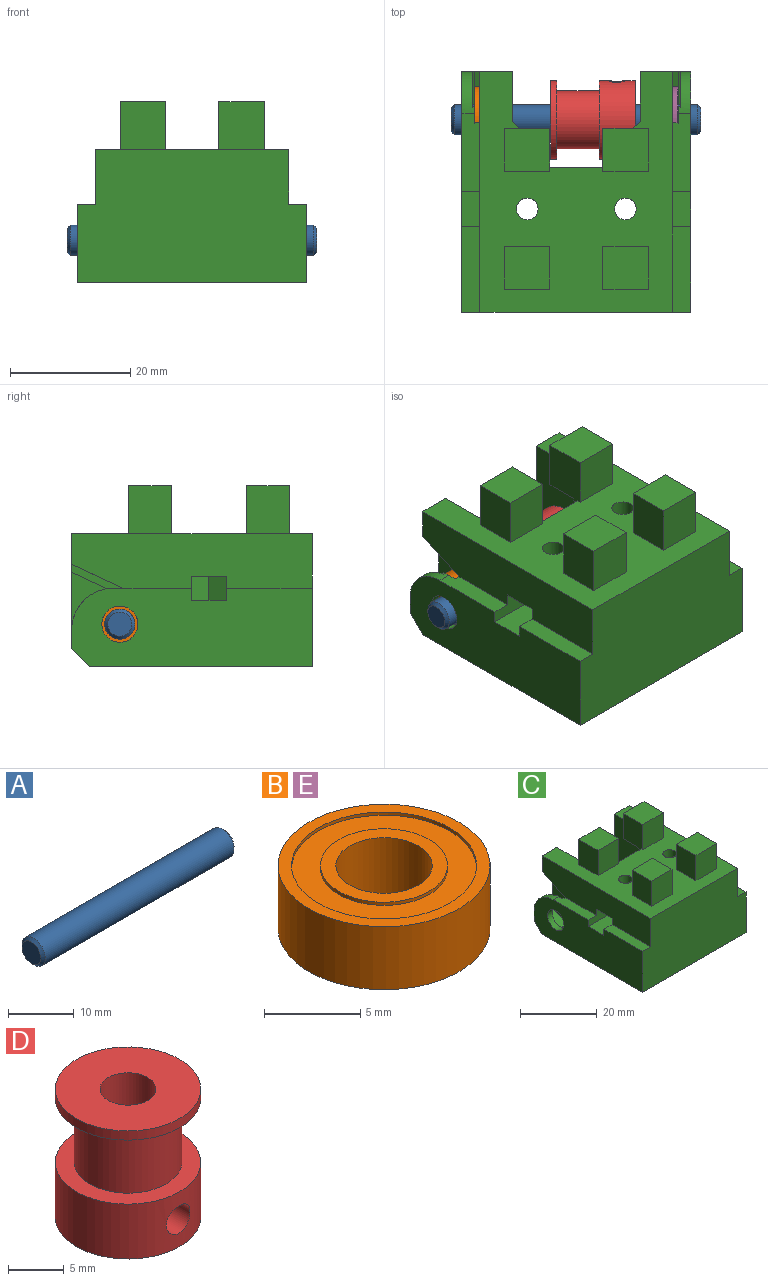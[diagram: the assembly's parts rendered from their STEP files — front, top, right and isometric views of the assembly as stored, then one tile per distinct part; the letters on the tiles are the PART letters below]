
ASSEMBLY  parts=5 mates=5
PART A: 5 faces, bbox 41.5x5x5 mm
  f0: cylinder r=2.5mm len=40.5mm, axis (-1,0,0), area 636.2mm2, adj f3,f4
  f1: plane 4x4mm, normal (1,0,0), area 12.6mm2, adj f3
  f2: plane 4x4mm, normal (-1,0,0), area 12.6mm2, adj f4
  f3: cone r=2mm half-angle=45deg, axis (-1,0,0), area 10mm2, adj f0,f1
  f4: cone r=2.5mm half-angle=45deg, axis (1,0,0), area 10mm2, adj f0,f2
PART B: 12 faces, bbox 11x11x4 mm
  f0: plane 6.6x6.6mm, normal (0,0,1), area 14.6mm2, adj f3,f9
  f1: plane 6.6x6.6mm, normal (0,0,-1), area 14.6mm2, adj f3,f6
  f2: cylinder r=5.5mm len=11mm, axis (0,0,-1), area 138.2mm2, adj f4,f5
  f3: cylinder r=2.5mm len=5mm, axis (0,0,-1), area 62.8mm2, adj f0,f1
  f4: plane 11x11mm, normal (0,0,1), area 22.7mm2, adj f2,f10
  f5: plane 11x11mm, normal (0,0,-1), area 22.7mm2, adj f2,f7
  f6: cylinder r=3.3mm len=6.6mm, axis (0,0,-1), area 4.1mm2, adj f1,f8
  f7: cylinder r=4.8mm len=9.6mm, axis (0,0,-1), area 6mm2, adj f5,f8
  f8: plane 9.6x9.6mm, normal (0,0,-1), area 38.2mm2, adj f6,f7
  f9: cylinder r=3.3mm len=6.6mm, axis (0,0,-1), area 4.1mm2, adj f0,f11
  f10: cylinder r=4.8mm len=9.6mm, axis (0,0,-1), area 6mm2, adj f4,f11
  f11: plane 9.6x9.6mm, normal (0,0,1), area 38.2mm2, adj f9,f10
PART C: 107 faces, bbox 38x40x30 mm
  f0: plane 39.96x13mm, normal (-1,0,0), area 464.6mm2, adj f3,f11,f15,f18,f72,f77,f80,f100
  f1: cylinder r=1.8mm len=7mm, axis (0,0,-1), area 79.2mm2, adj f5,f97
  f2: cylinder r=1.8mm len=7mm, axis (0,0,-1), area 79.2mm2, adj f5,f99
  f3: plane 12.9x3mm, normal (0,0,1), area 37.3mm2, adj f0,f8,f55,f76,f100,f105
  f4: plane 12.9x3mm, normal (0,0,1), area 37.3mm2, adj f6,f50,f53,f78,f94,f106
  f5: plane 39.96x32mm, normal (0,0,1), area 785.9mm2, adj f1,f2,f7,f11,f12,f13,f14,f15
  f6: plane 39.96x13mm, normal (1,0,0), area 464.6mm2, adj f4,f7,f15,f18,f75,f79,f81,f94
  f7: plane 19x8.4mm, normal (0,1,0), area 61.1mm2, adj f5,f6,f12,f49,f50,f52,f53,f58
  f8: plane 13.65x11.65mm, normal (1,0,0), area 30.5mm2, adj f3,f9,f11,f54,f55,f56,f70,f71
  f9: plane 4.02x1.87mm, normal (0,0.42,-0.91), area 1.8mm2, adj f8,f10,f70,f105
  f10: plane 12.45x10.36mm, normal (1,0,0), area 65.5mm2, adj f9,f11,f70,f71,f72,f105
  f11: plane 19x8.4mm, normal (0,1,0), area 61.1mm2, adj f0,f5,f8,f10,f14,f54,f55,f57
  f12: plane 20.8x16mm, normal (-1,0,0), area 289.1mm2, adj f5,f7,f13,f74,f82,f83,f88,f91
  f13: plane 21.2x20.8mm, normal (0,1,0), area 426.1mm2, adj f5,f12,f14,f31,f36,f84,f87,f89
  f14: plane 20.8x16mm, normal (1,0,0), area 289.1mm2, adj f5,f11,f13,f73,f85,f86,f90,f92
  f15: plane 38x22mm, normal (0,-1,0), area 782mm2, adj f0,f5,f6,f18,f76,f77,f78,f79
  f16: cylinder r=1.8mm len=11mm, axis (0,0,-1), area 124.4mm2, adj f18,f98
  f17: cylinder r=1.8mm len=11mm, axis (0,0,-1), area 124.4mm2, adj f18,f104
  f18: plane 38x36.96mm, normal (0,0,-1), area 803.8mm2, adj f0,f6,f15,f16,f17,f41,f42,f43
  f19: plane 8x7.6mm, normal (0,1,0), area 60.8mm2, adj f5,f20,f22,f23
  f20: plane 8x7.1mm, normal (-1,0,0), area 56.8mm2, adj f5,f19,f21,f23
  f21: plane 8x7.6mm, normal (0,-1,0), area 60.8mm2, adj f5,f20,f22,f23
  f22: plane 8x7.1mm, normal (1,0,0), area 56.8mm2, adj f5,f19,f21,f23
  f23: plane 7.6x7.1mm, normal (0,0,1), area 54mm2, adj f19,f20,f21,f22
  f24: plane 8x7.6mm, normal (0,1,0), area 60.8mm2, adj f5,f25,f27,f28
  f25: plane 8x7.1mm, normal (-1,0,0), area 56.8mm2, adj f5,f24,f26,f28
  f26: plane 8x7.6mm, normal (0,-1,0), area 60.8mm2, adj f5,f25,f27,f28
  f27: plane 8x7.1mm, normal (1,0,0), area 56.8mm2, adj f5,f24,f26,f28
  f28: plane 7.6x7.1mm, normal (0,0,1), area 54mm2, adj f24,f25,f26,f27
  f29: plane 5.35x5mm, normal (0,0,-1), area 26.7mm2, adj f30,f31,f87,f88
  f30: plane 8x7.6mm, normal (0,1,0), area 60.8mm2, adj f5,f29,f31,f33,f34
  f31: plane 9.2x7.1mm, normal (-1,0,0), area 57.5mm2, adj f5,f13,f29,f30,f32,f34,f87
  f32: plane 8x7.6mm, normal (0,-1,0), area 60.8mm2, adj f5,f31,f33,f34
  f33: plane 8x7.1mm, normal (1,0,0), area 56.8mm2, adj f5,f30,f32,f34
  f34: plane 7.6x7.1mm, normal (0,0,1), area 54mm2, adj f30,f31,f32,f33
  f35: plane 8x7.6mm, normal (0,-1,0), area 60.8mm2, adj f5,f36,f38,f39
  f36: plane 9.2x7.1mm, normal (1,0,0), area 57.5mm2, adj f5,f13,f35,f37,f39,f40,f89
  f37: plane 8x7.6mm, normal (0,1,0), area 60.8mm2, adj f5,f36,f38,f39,f40
  f38: plane 8x7.1mm, normal (-1,0,0), area 56.8mm2, adj f5,f35,f37,f39
  f39: plane 7.6x7.1mm, normal (0,0,1), area 54mm2, adj f35,f36,f37,f38
  f40: plane 5.35x5mm, normal (0,0,-1), area 26.8mm2, adj f36,f37,f89,f90
  f41: plane 20x15mm, normal (0.47,0.88,0), area 339.8mm2, adj f18,f42,f47,f48
  f42: plane 20x8.39mm, normal (0.38,-0.92,0), area 181.6mm2, adj f18,f41,f43,f48
  f43: cylinder r=4mm len=20mm, axis (0,0,-1), area 46mm2, adj f18,f42,f44,f48
  f44: plane 20x7.07mm, normal (0.82,-0.57,0), area 171.4mm2, adj f18,f43,f45,f48
  f45: plane 20x8.04mm, normal (-0.82,-0.57,0), area 195.1mm2, adj f18,f44,f46,f48
  f46: plane 20x9.48mm, normal (-0.38,-0.92,0), area 205.3mm2, adj f18,f45,f47,f48
  f47: plane 20x15mm, normal (-0.47,0.88,0), area 339.8mm2, adj f18,f41,f46,f48
  f48: plane 30x19.96mm, normal (0,0,-1), area 245mm2, adj f41,f42,f43,f44,f45,f46,f47
  f49: plane 6.07x4.2mm, normal (0,-0.34,0.94), area 27.1mm2, adj f7,f51,f52,f53
  f50: plane 10.39x4.84mm, normal (0,0.42,-0.91), area 39.7mm2, adj f4,f7,f51,f52,f53,f78
  f51: cylinder r=5.65mm len=10.77mm, axis (1,0,0), area 72.5mm2, adj f49,f50,f52,f53
  f52: plane 15.61x13.65mm, normal (1,0,0), area 39.9mm2, adj f7,f49,f50,f51,f62,f63,f64
  f53: plane 13.65x11.65mm, normal (-1,0,0), area 30.5mm2, adj f4,f7,f49,f50,f51,f58,f59,f60
  f54: plane 6.07x4.2mm, normal (0,-0.34,0.94), area 27.1mm2, adj f8,f11,f56,f57
  f55: plane 10.39x4.84mm, normal (0,0.42,-0.91), area 39.7mm2, adj f3,f8,f11,f56,f57,f76
  f56: cylinder r=5.65mm len=10.77mm, axis (1,0,0), area 72.5mm2, adj f8,f54,f55,f57
  f57: plane 15.61x13.65mm, normal (-1,0,0), area 39.9mm2, adj f11,f54,f55,f56,f66,f67,f68
  f58: plane 6.48x2.36mm, normal (0,-0.34,0.94), area 2.8mm2, adj f7,f53,f59,f61
  f59: cylinder r=4.45mm len=8.48mm, axis (1,0,0), area 5.4mm2, adj f53,f58,f60,f61
  f60: plane 4.02x1.87mm, normal (0,0.42,-0.91), area 1.8mm2, adj f53,f59,f61,f106
  f61: plane 12.45x10.36mm, normal (-1,0,0), area 65.5mm2, adj f7,f58,f59,f60,f75,f106
  f62: plane 9.88x4.61mm, normal (0,0.42,-0.91), area 4.4mm2, adj f7,f52,f63,f65
  f63: cylinder r=4.45mm len=8.48mm, axis (1,0,0), area 5.4mm2, adj f52,f62,f64,f65
  f64: plane 6.48x2.36mm, normal (0,-0.34,0.94), area 2.8mm2, adj f7,f52,f63,f65
  f65: plane 13.09x12.45mm, normal (1,0,0), area 83.4mm2, adj f7,f62,f63,f64,f74
  f66: plane 6.48x2.36mm, normal (0,-0.34,0.94), area 2.8mm2, adj f11,f57,f67,f69
  f67: cylinder r=4.45mm len=8.48mm, axis (1,0,0), area 5.4mm2, adj f57,f66,f68,f69
  f68: plane 9.88x4.61mm, normal (0,0.42,-0.91), area 4.4mm2, adj f11,f57,f67,f69
  f69: plane 13.09x12.45mm, normal (-1,0,0), area 83.4mm2, adj f11,f66,f67,f68,f73
  f70: cylinder r=4.45mm len=8.48mm, axis (1,0,0), area 5.4mm2, adj f8,f9,f10,f71
  f71: plane 6.48x2.36mm, normal (0,-0.34,0.94), area 2.8mm2, adj f8,f10,f11,f70
  f72: cylinder r=3mm len=6mm, axis (1,0,0), area 32mm2, adj f0,f10
  f73: cylinder r=3mm len=6mm, axis (1,0,0), area 32mm2, adj f14,f69
  f74: cylinder r=3mm len=6mm, axis (1,0,0), area 32mm2, adj f12,f65
  f75: cylinder r=3mm len=6mm, axis (1,0,0), area 32mm2, adj f6,f61
  f76: plane 39.96x9mm, normal (-1,0,0), area 331.2mm2, adj f3,f5,f11,f15,f55,f77,f99,f100
  f77: plane 14.26x3mm, normal (0,0,1), area 42.8mm2, adj f0,f15,f76,f101
  f78: plane 39.96x9mm, normal (1,0,0), area 331.2mm2, adj f4,f5,f7,f15,f50,f79,f94,f95
  f79: plane 14.26x3mm, normal (0,0,1), area 42.8mm2, adj f6,f15,f78,f95
  f80: plane 7.2x3mm, normal (0,0.71,-0.71), area 30.5mm2, adj f0,f11,f18,f86
  f81: plane 7.2x3mm, normal (0,0.71,-0.71), area 30.5mm2, adj f6,f7,f18,f82
  f82: plane 4.7x3.5mm, normal (-0.71,0.5,-0.5), area 7.8mm2, adj f7,f12,f81,f83
  f83: plane 14.2x1.2mm, normal (-0.71,0,-0.71), area 22.7mm2, adj f12,f18,f82,f84
  f84: plane 23.6x1.2mm, normal (0,0.71,-0.71), area 38mm2, adj f13,f18,f83,f85
  f85: plane 14.2x1.2mm, normal (0.71,0,-0.71), area 22.7mm2, adj f14,f18,f84,f86
  f86: plane 4.7x3.5mm, normal (0.71,0.5,-0.5), area 7.8mm2, adj f11,f14,f80,f85
  f87: plane 6.2x1.2mm, normal (0,0.71,-0.71), area 9.5mm2, adj f13,f29,f31,f88
  f88: plane 7.75x1.2mm, normal (-0.71,0,-0.71), area 11.1mm2, adj f12,f29,f87,f91
  f89: plane 6.2x1.2mm, normal (0,0.71,-0.71), area 9.5mm2, adj f13,f36,f40,f90
  f90: plane 7.75x1.2mm, normal (0.71,0,-0.71), area 11.1mm2, adj f14,f40,f89,f92
  f91: plane 1.2x1.2mm, normal (-0.71,0.71,0), area 1mm2, adj f5,f12,f88
  f92: plane 1.2x1.2mm, normal (0.71,0.71,0), area 1mm2, adj f5,f14,f90
  f93: plane 4x2.9mm, normal (0.87,-0.5,0), area 13.4mm2, adj f94,f96,f97,f98
  f94: plane 12.52x4mm, normal (0,-1,0), area 44.1mm2, adj f4,f6,f78,f93,f97,f98
  f95: plane 12.52x4mm, normal (0,1,0), area 44.1mm2, adj f6,f78,f79,f96,f97,f98
  f96: plane 4x2.9mm, normal (0.87,0.5,0), area 13.4mm2, adj f93,f95,f97,f98
  f97: plane 11.2x5.8mm, normal (0,0,-1), area 49.9mm2, adj f1,f78,f93,f94,f95,f96
  f98: plane 14.2x5.8mm, normal (0,0,1), area 67.3mm2, adj f6,f16,f93,f94,f95,f96
  f99: plane 11.2x5.8mm, normal (0,0,-1), area 49.9mm2, adj f2,f76,f100,f101,f102,f103
  f100: plane 12.52x4mm, normal (0,-1,0), area 44.1mm2, adj f0,f3,f76,f99,f102,f104
  f101: plane 12.52x4mm, normal (0,1,0), area 44.1mm2, adj f0,f76,f77,f99,f103,f104
  f102: plane 4x2.9mm, normal (-0.87,-0.5,0), area 13.4mm2, adj f99,f100,f103,f104
  f103: plane 4x2.9mm, normal (-0.87,0.5,0), area 13.4mm2, adj f99,f101,f102,f104
  f104: plane 14.2x5.8mm, normal (0,0,1), area 67.3mm2, adj f0,f17,f100,f101,f102,f103
  f105: cylinder r=7mm len=7mm, axis (1,0,0), area 19.1mm2, adj f0,f3,f8,f9,f10,f11
  f106: cylinder r=7mm len=7mm, axis (-1,0,0), area 19.1mm2, adj f4,f6,f7,f53,f60,f61
PART D: 10 faces, bbox 13x13x14 mm
  f0: cylinder r=2.5mm len=14mm, axis (0,0,1), area 205.1mm2, adj f2,f7,f8,f9
  f1: cylinder r=6.5mm len=13mm, axis (0,0,1), area 230.8mm2, adj f2,f3,f8,f9
  f2: plane 13x13mm, normal (0,0,-1), area 113.1mm2, adj f0,f1
  f3: plane 13x13mm, normal (0,0,1), area 60.3mm2, adj f1,f4
  f4: cylinder r=4.8mm len=9.6mm, axis (0,0,1), area 211.1mm2, adj f3,f5
  f5: plane 13x13mm, normal (0,0,-1), area 60.3mm2, adj f4,f6
  f6: cylinder r=6.5mm len=13mm, axis (0,0,1), area 40.8mm2, adj f5,f7
  f7: plane 13x13mm, normal (0,0,1), area 113.1mm2, adj f0,f6
  f8: cylinder r=1.5mm len=4.5mm, axis (0,1,0), area 39.2mm2, adj f0,f1
  f9: cylinder r=1.5mm len=4.5mm, axis (-1,0,0), area 39.2mm2, adj f0,f1
PART E: same geometry as B
PLACE A at identity fixed
PLACE B rot(axis=(0,-1,0),90deg) t=(-12.8,0,0)mm
PLACE C t=(0.05,-14.8,-7)mm
PLACE D rot(axis=(-0.71,-0.03,0.71),176.9deg) t=(9.83,0,0)mm
PLACE E rot(axis=(0,1,0),90deg) t=(12.9,0,0)mm
MATE cylindrical D.f0 <-> A.f0  axis (-1,0,0) through (-4.17,0,0)mm
MATE slider E.f3 <-> A.f0  axis (1,0,0) through (16.9,0,0)mm
MATE revolute B.f2 <-> C.f51  axis (-1,0,0) through (-16.8,0,0)mm
MATE slider B.f3 <-> A.f0  axis (-1,0,0) through (-16.8,0,0)mm
MATE revolute E.f2 <-> C.f51  axis (1,0,0) through (16.9,0,0)mm
